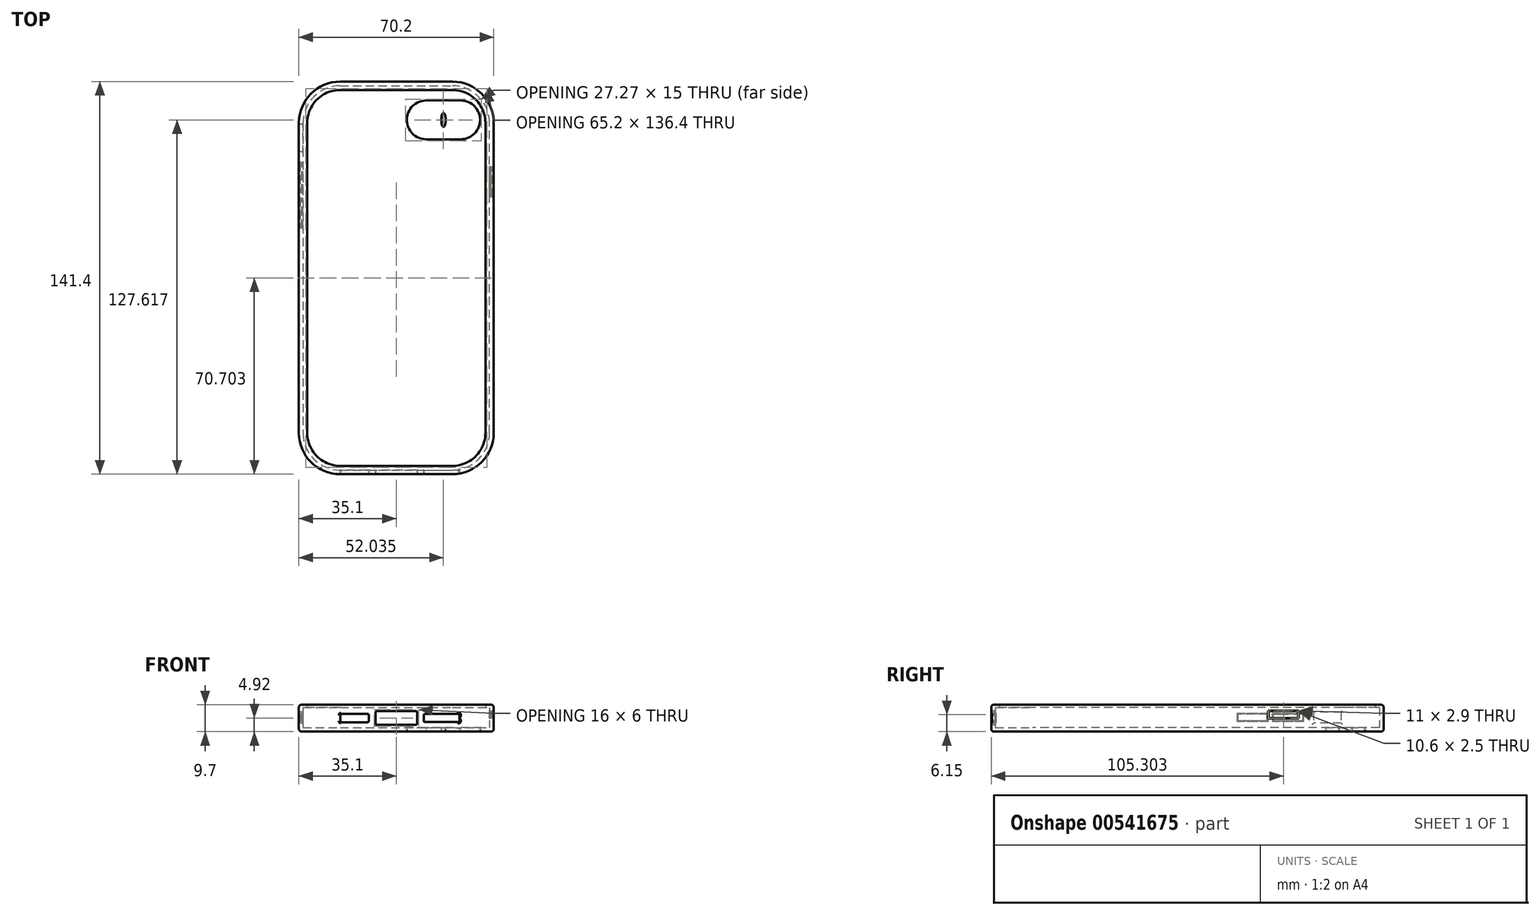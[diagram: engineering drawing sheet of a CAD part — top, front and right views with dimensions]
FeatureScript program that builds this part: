
annotation { "Feature Type Name" : "Feature", "Feature Type Description" : "" }
export const myFeature = defineFeature(function(context is Context, id is Id, definition is map)
    precondition{}
    {
        {
            var Q0;
            Q0=qCreatedBy(makeId("Top.planeOp"),FACE);
            var sketch = newSketch(context, id + "F0", { "sketchPlane" : qUnion([Q0])});
            skArc(sketch, "E0", {"start": v(-23.7, 70.7) * mm, "mid": v(-33.18, 66.77) * mm, "end": v(-37.1, 57.3) * mm});
            skArc(sketch, "E1", {"start": v(-37.1, -54.3) * mm, "mid": v(-33.18, -63.78) * mm, "end": v(-23.7, -67.7) * mm});
            skArc(sketch, "E2", {"start": v(16.7, -67.7) * mm, "mid": v(26.18, -63.78) * mm, "end": v(30.1, -54.3) * mm});
            skArc(sketch, "E3", {"start": v(30.1, 57.3) * mm, "mid": v(26.18, 66.77) * mm, "end": v(16.7, 70.7) * mm});
            skLineSegment(sketch, "E4", {"start": v(-23.7, -67.7) * mm, "end": v(16.7, -67.7) * mm});
            skLineSegment(sketch, "E5", {"start": v(30.1, -54.3) * mm, "end": v(30.1, 57.3) * mm});
            skLineSegment(sketch, "E6", {"start": v(-37.1, 57.3) * mm, "end": v(-37.1, -54.3) * mm});
            skLineSegment(sketch, "E7", {"start": v(-23.7, 70.7) * mm, "end": v(16.7, 70.7) * mm});
            skLineSegment(sketch, "E8.0", {"start": v(-23.7, 72.2) * mm, "end": v(16.7, 72.2) * mm});
            skArc(sketch, "E8.1", {"start": v(31.6, 57.3) * mm, "mid": v(27.24, 67.83) * mm, "end": v(16.7, 72.2) * mm});
            skArc(sketch, "E8.2", {"start": v(-23.7, 72.2) * mm, "mid": v(-34.24, 67.83) * mm, "end": v(-38.6, 57.3) * mm});
            skLineSegment(sketch, "E8.3", {"start": v(31.6, -54.3) * mm, "end": v(31.6, 57.3) * mm});
            skLineSegment(sketch, "E8.4", {"start": v(-38.6, 57.3) * mm, "end": v(-38.6, -54.3) * mm});
            skArc(sketch, "E8.5", {"start": v(-38.6, -54.3) * mm, "mid": v(-34.24, -64.84) * mm, "end": v(-23.7, -69.2) * mm});
            skLineSegment(sketch, "E8.6", {"start": v(-23.7, -69.2) * mm, "end": v(16.7, -69.2) * mm});
            skArc(sketch, "E8.7", {"start": v(16.7, -69.2) * mm, "mid": v(27.24, -64.84) * mm, "end": v(31.6, -54.3) * mm});
            skLineSegment(sketch, "E9", {"start": v(-37.1, -54.3) * mm, "end": v(-3.5, -54.3) * mm, "construction": true});
            skLineSegment(sketch, "E10", {"start": v(-3.5, -54.3) * mm, "end": v(-3.5, -67.7) * mm, "construction": true});
            skSolve(sketch);
        }
        {
            var Q0;
            Q0=makeQuery(id+"F0.imprint","IMPRINT",FACE,{"disambiguationData":[TD([[makeQuery(id+"F0.imprint","IMPRINT",EDGE,{"derivedFrom":sQuery(id+"F0.wireOp",EDGE,"E0")}),-1.0]])]});
            extrude(context, id + "F1", {"entities" : qUnion([Q0]), "depth" : 8.2 * mm, "offsetDistance" : 25 * mm});
        }
        {
            var Q0;
            Q0=makeQuery(id+"F0.imprint","IMPRINT",FACE,{"disambiguationData":[TD([[makeQuery(id+"F0.imprint","IMPRINT",EDGE,{"derivedFrom":sQuery(id+"F0.wireOp",EDGE,"E0")}),1.0]])]});
            var Q1;
            Q1=makeQuery(id+"F0.imprint","IMPRINT",FACE,{"disambiguationData":[TD([[makeQuery(id+"F0.imprint","IMPRINT",EDGE,{"derivedFrom":sQuery(id+"F0.wireOp",EDGE,"E0")}),-1.0]])]});
            extrude(context, id + "F2", {"entities" : qUnion([Q0, Q1]), "operationType" : NewBodyOperationType.ADD, "oppositeDirection" : true, "depth" : 1.5 * mm, "offsetDistance" : 25 * mm});
        }
        {
            var Q0;
            {var subQ0=sQuery(id+"F0.wireOp",EDGE,"E8.6");Q0=makeQuery(id+"F2.boolean.opBoolean","MERGE",FACE,{"derivedFrom":[makeQuery(id+"F1.opExtrude","SWEPT_FACE",FACE,{"disambiguationData":[OSD([subQ0])]}),makeQuery(id+"F2.opExtrude","SWEPT_FACE",FACE,{"disambiguationData":[OSD([subQ0])]})]});}
            var sketch = newSketch(context, id + "F3", { "sketchPlane" : qUnion([Q0])});
            skLineSegment(sketch, "E11", {"start": v(-23.7, 3.42) * mm, "end": v(16.7, 3.42) * mm, "construction": true});
            skLineSegment(sketch, "E12", {"start": v(-3.5, -1.5) * mm, "end": v(-3.5, 8.2) * mm, "construction": true});
            skLineSegment(sketch, "E13.bottom", {"start": v(-11, 5.92) * mm, "end": v(4, 5.92) * mm});
            skLineSegment(sketch, "E13.top", {"start": v(-11, 0.92) * mm, "end": v(4, 0.92) * mm});
            skLineSegment(sketch, "E13.left", {"start": v(-11, 5.92) * mm, "end": v(-11, 0.92) * mm});
            skLineSegment(sketch, "E13.right", {"start": v(4, 5.92) * mm, "end": v(4, 0.92) * mm});
            skPoint(sketch, "E13.middle", {"position": v(-3.5, 3.42) * mm});
            skLineSegment(sketch, "E14.bottom", {"start": v(-23.7, 3.42) * mm, "end": v(-10.9, 3.42) * mm});
            skLineSegment(sketch, "E14.top", {"start": v(-26.2, 4.92) * mm, "end": v(-13.4, 4.92) * mm});
            skLineSegment(sketch, "E14.left", {"start": v(-26.2, 3.42) * mm, "end": v(-26.2, 4.92) * mm});
            skLineSegment(sketch, "E14.right", {"start": v(-13.4, 3.42) * mm, "end": v(-13.4, 4.92) * mm});
            skLineSegment(sketch, "E15.top", {"start": v(-26.2, 1.87) * mm, "end": v(-13.4, 1.87) * mm});
            skLineSegment(sketch, "E15.left", {"start": v(-26.2, 3.42) * mm, "end": v(-26.2, 1.87) * mm});
            skLineSegment(sketch, "E15.right", {"start": v(-13.4, 3.42) * mm, "end": v(-13.4, 1.87) * mm});
            skLineSegment(sketch, "E16.bottom", {"start": v(19.2, 3.42) * mm, "end": v(6.4, 3.42) * mm});
            skLineSegment(sketch, "E16.top", {"start": v(19.2, 4.92) * mm, "end": v(6.4, 4.92) * mm});
            skLineSegment(sketch, "E16.left", {"start": v(19.2, 3.42) * mm, "end": v(19.2, 4.92) * mm});
            skLineSegment(sketch, "E16.right", {"start": v(6.4, 3.42) * mm, "end": v(6.4, 4.92) * mm});
            skLineSegment(sketch, "E17.top", {"start": v(19.2, 1.92) * mm, "end": v(6.4, 1.92) * mm});
            skLineSegment(sketch, "E17.left", {"start": v(19.2, 3.42) * mm, "end": v(19.2, 1.92) * mm});
            skLineSegment(sketch, "E17.right", {"start": v(6.4, 3.42) * mm, "end": v(6.4, 1.92) * mm});
            skSolve(sketch);
        }
        {
            var Q0;
            Q0=makeQuery(id+"F3.imprint","IMPRINT",FACE,{"disambiguationData":[TD([[makeQuery(id+"F3.imprint","IMPRINT",EDGE,{"derivedFrom":sQuery(id+"F3.wireOp",EDGE,"E14.bottom")}),-1.0]])]});
            var Q1;
            Q1=makeQuery(id+"F3.imprint","IMPRINT",FACE,{"disambiguationData":[TD([[makeQuery(id+"F3.imprint","IMPRINT",EDGE,{"derivedFrom":sQuery(id+"F3.wireOp",EDGE,"E14.top")}),-1.0]])]});
            var Q2;
            Q2=makeQuery(id+"F3.imprint","IMPRINT",FACE,{"disambiguationData":[TD([[makeQuery(id+"F3.imprint","IMPRINT",EDGE,{"derivedFrom":sQuery(id+"F3.wireOp",EDGE,"E13.bottom")}),-1.0]])]});
            var Q3;
            Q3=makeQuery(id+"F3.imprint","IMPRINT",FACE,{"disambiguationData":[TD([[makeQuery(id+"F3.imprint","IMPRINT",EDGE,{"derivedFrom":sQuery(id+"F3.wireOp",EDGE,"E16.top")}),1.0]])]});
            var Q4;
            Q4=makeQuery(id+"F3.imprint","IMPRINT",FACE,{"disambiguationData":[TD([[makeQuery(id+"F3.imprint","IMPRINT",EDGE,{"derivedFrom":sQuery(id+"F3.wireOp",EDGE,"E16.bottom")}),1.0]])]});
            extrude(context, id + "F4", {"entities" : qUnion([Q0, Q1, Q2, Q3, Q4]), "operationType" : NewBodyOperationType.REMOVE, "oppositeDirection" : true, "depth" : 3 * mm, "offsetDistance" : 25 * mm});
        }
        {
            var Q0;
            Q0=makeQuery(id+"F2.opExtrude","CAP_FACE",FACE,{"disambiguationData":[OSD([sQuery(id+"F0.wireOp",EDGE,"E8.0"),sQuery(id+"F0.wireOp",EDGE,"E8.1"),sQuery(id+"F0.wireOp",EDGE,"E8.2"),sQuery(id+"F0.wireOp",EDGE,"E8.3"),sQuery(id+"F0.wireOp",EDGE,"E8.4"),sQuery(id+"F0.wireOp",EDGE,"E8.5"),sQuery(id+"F0.wireOp",EDGE,"E8.6"),sQuery(id+"F0.wireOp",EDGE,"E8.7")])],"isStart":false});
            var sketch = newSketch(context, id + "F5", { "sketchPlane" : qUnion([Q0])});
            skCircle(sketch, "E18", {"center": v(19.7, -58.4) * mm, "radius": 7 * mm});
            skCircle(sketch, "E19.1.0.0", {"center": v(7.3, -58.4) * mm, "radius": 7 * mm});
            skLineSegment(sketch, "E19.direction1", {"start": v(19.7, -58.4) * mm, "end": v(7.3, -58.4) * mm, "construction": true});
            skLineSegment(sketch, "E20", {"start": v(19.75, -65.4) * mm, "end": v(7.3, -65.4) * mm});
            skLineSegment(sketch, "E21", {"start": v(7.2, -51.4) * mm, "end": v(19.7, -51.4) * mm});
            skSolve(sketch);
        }
        {
            var Q0;
            {var subQ0=sQuery(id+"F5.wireOp",EDGE,"E18");var subQ3=makeQuery(id+"F5.imprint","IMPRINT",VERTEX,{"derivedFrom":subQ0});Q0=makeQuery(id+"F5.imprint","IMPRINT",FACE,{"disambiguationData":[TD([[makeQuery(id+"F5.imprint","IMPRINT",EDGE,{"disambiguationData":[TD([[subQ3,1.0]])],"derivedFrom":subQ0}),1.0]])]});}
            var Q1;
            {var subQ0=sQuery(id+"F5.wireOp",EDGE,"E19.1.0.0");var subQ1=makeQuery(id+"F5.imprint","INTERSECT",VERTEX,{"derivedFrom":[subQ0,sQuery(id+"F5.wireOp",EDGE,"E20")]});Q1=makeQuery(id+"F5.imprint","IMPRINT",FACE,{"disambiguationData":[TD([[makeQuery(id+"F5.imprint","IMPRINT",EDGE,{"disambiguationData":[TD([[subQ1,1.0]])],"derivedFrom":subQ0}),1.0]])]});}
            var Q2;
            {var subQ0=sQuery(id+"F5.wireOp",EDGE,"E20");Q2=makeQuery(id+"F5.imprint","IMPRINT",FACE,{"disambiguationData":[TD([[makeQuery(id+"F5.imprint","IMPRINT",EDGE,{"derivedFrom":subQ0}),-1.0]])]});}
            var Q3;
            {var subQ0=sQuery(id+"F5.wireOp",EDGE,"E19.1.0.0");var subQ1=sQuery(id+"F5.wireOp",EDGE,"E18");var subQ2=makeQuery(id+"F5.imprint","INTERSECT",VERTEX,{"disambiguationData":[OD(0.0)],"derivedFrom":[subQ1,subQ0]});Q3=makeQuery(id+"F5.imprint","IMPRINT",FACE,{"disambiguationData":[TD([[makeQuery(id+"F5.imprint","IMPRINT",EDGE,{"disambiguationData":[TD([[subQ2,-1.0]])],"derivedFrom":subQ1}),1.0]])]});}
            var Q4;
            {var subQ0=sQuery(id+"F5.wireOp",EDGE,"E21");var subQ1=sQuery(id+"F5.wireOp",EDGE,"E18");var subQ2=makeQuery(id+"F5.imprint","INTERSECT",VERTEX,{"derivedFrom":[subQ1,subQ0]});Q4=makeQuery(id+"F5.imprint","IMPRINT",FACE,{"disambiguationData":[TD([[makeQuery(id+"F5.imprint","IMPRINT",EDGE,{"disambiguationData":[TD([[subQ2,-1.0]])],"derivedFrom":subQ1}),-1.0]])]});}
            extrude(context, id + "F6", {"entities" : qUnion([Q0, Q1, Q2, Q3, Q4]), "operationType" : NewBodyOperationType.REMOVE, "oppositeDirection" : true, "depth" : 5 * mm, "offsetDistance" : 25 * mm});
        }
        {
            var Q0;
            Q0=makeQuery(id+"F1.opExtrude","SWEPT_FACE",FACE,{"disambiguationData":[OSD([sQuery(id+"F0.wireOp",EDGE,"E5")])]});
            var sketch = newSketch(context, id + "F7", { "sketchPlane" : qUnion([Q0])});
            skLineSegment(sketch, "E22", {"start": v(-57.3, 4.65) * mm, "end": v(-33.08, 4.65) * mm, "construction": true});
            skLineSegment(sketch, "E23", {"start": v(-36.1, 8.2) * mm, "end": v(-36.1, 0) * mm, "construction": true});
            skLineSegment(sketch, "E24.bottom", {"start": v(-36.1, 4.65) * mm, "end": v(-41.4, 4.65) * mm});
            skLineSegment(sketch, "E24.top", {"start": v(-36.1, 5.9) * mm, "end": v(-41.4, 5.9) * mm});
            skLineSegment(sketch, "E24.left", {"start": v(-36.1, 4.65) * mm, "end": v(-36.1, 5.9) * mm});
            skLineSegment(sketch, "E24.right", {"start": v(-41.4, 4.65) * mm, "end": v(-41.4, 5.9) * mm});
            skLineSegment(sketch, "E25.top", {"start": v(-36.1, 3.4) * mm, "end": v(-41.4, 3.4) * mm});
            skLineSegment(sketch, "E25.left", {"start": v(-36.1, 4.65) * mm, "end": v(-36.1, 3.4) * mm});
            skLineSegment(sketch, "E25.right", {"start": v(-41.4, 4.65) * mm, "end": v(-41.4, 3.4) * mm});
            skLineSegment(sketch, "E26.bottom", {"start": v(-41.4, 5.9) * mm, "end": v(-30.8, 5.9) * mm});
            skLineSegment(sketch, "E26.top", {"start": v(-41.4, 3.4) * mm, "end": v(-30.8, 3.4) * mm});
            skLineSegment(sketch, "E26.right", {"start": v(-30.8, 5.9) * mm, "end": v(-30.8, 3.4) * mm});
            skPoint(sketch, "E26.middle", {"position": v(-36.1, 4.65) * mm});
            skLineSegment(sketch, "E27.0", {"start": v(-41.6, 6.1) * mm, "end": v(-30.6, 6.1) * mm});
            skLineSegment(sketch, "E27.1", {"start": v(-41.6, 4.65) * mm, "end": v(-41.6, 6.1) * mm});
            skLineSegment(sketch, "E27.2", {"start": v(-30.6, 6.1) * mm, "end": v(-30.6, 3.2) * mm});
            skLineSegment(sketch, "E27.3", {"start": v(-41.6, 3.2) * mm, "end": v(-30.6, 3.2) * mm});
            skLineSegment(sketch, "E27.4", {"start": v(-41.6, 4.65) * mm, "end": v(-41.6, 3.2) * mm});
            skSolve(sketch);
        }
        {
            var Q0;
            {var subQ4=sQuery(id+"F7.wireOp",EDGE,"E24.right");Q0=makeQuery(id+"F7.imprint","IMPRINT",FACE,{"disambiguationData":[TD([[makeQuery(id+"F7.imprint","IMPRINT",EDGE,{"derivedFrom":subQ4}),1.0]])]});}
            extrude(context, id + "F8", {"entities" : qUnion([Q0]), "operationType" : NewBodyOperationType.REMOVE, "oppositeDirection" : true, "depth" : .5 * mm, "offsetDistance" : 25 * mm});
        }
        {
            var Q0;
            {var subQ0=sQuery(id+"F0.wireOp",EDGE,"E8.3");Q0=makeQuery(id+"F2.boolean.opBoolean","MERGE",FACE,{"derivedFrom":[makeQuery(id+"F1.opExtrude","SWEPT_FACE",FACE,{"disambiguationData":[OSD([subQ0])]}),makeQuery(id+"F2.opExtrude","SWEPT_FACE",FACE,{"disambiguationData":[OSD([subQ0])]})]});}
            var sketch = newSketch(context, id + "F9", { "sketchPlane" : qUnion([Q0])});
            skLineSegment(sketch, "E28.bottom", {"start": v(30.8, 5.9) * mm, "end": v(41.4, 5.9) * mm});
            skLineSegment(sketch, "E28.top", {"start": v(30.8, 3.4) * mm, "end": v(41.4, 3.4) * mm});
            skLineSegment(sketch, "E28.right", {"start": v(41.4, 5.9) * mm, "end": v(41.4, 3.4) * mm});
            skLineSegment(sketch, "E29", {"start": v(30.8, 5.9) * mm, "end": v(30.8, 3.4) * mm});
            skLineSegment(sketch, "E30.0", {"start": v(41.6, 6.1) * mm, "end": v(41.6, 3.2) * mm});
            skLineSegment(sketch, "E30.1", {"start": v(30.6, 6.1) * mm, "end": v(41.6, 6.1) * mm});
            skLineSegment(sketch, "E30.2", {"start": v(30.6, 6.1) * mm, "end": v(30.6, 3.2) * mm});
            skLineSegment(sketch, "E30.3", {"start": v(30.6, 3.2) * mm, "end": v(41.6, 3.2) * mm});
            skLineSegment(sketch, "E31.0", {"start": v(-59.3, 13.2) * mm, "end": v(-59.3, -6.5) * mm});
            skLineSegment(sketch, "E31.1", {"start": v(62.3, 13.2) * mm, "end": v(-59.3, 13.2) * mm});
            skLineSegment(sketch, "E31.2", {"start": v(62.3, -6.5) * mm, "end": v(62.3, 13.2) * mm});
            skLineSegment(sketch, "E31.3", {"start": v(-59.3, -6.5) * mm, "end": v(62.3, -6.5) * mm});
            skSolve(sketch);
        }
        {
            var Q0;
            Q0=makeQuery(id+"F9.imprint","IMPRINT",FACE,{"disambiguationData":[TD([[makeQuery(id+"F9.imprint","IMPRINT",EDGE,{"derivedFrom":sQuery(id+"F9.wireOp",EDGE,"E28.bottom")}),1.0]])]});
            extrude(context, id + "F10", {"entities" : qUnion([Q0]), "operationType" : NewBodyOperationType.REMOVE, "oppositeDirection" : true, "depth" : .5 * mm, "offsetDistance" : 25 * mm});
        }
        {
            var Q0;
            {var subQ0=sQuery(id+"F0.wireOp",EDGE,"E8.4");Q0=makeQuery(id+"F2.boolean.opBoolean","MERGE",FACE,{"derivedFrom":[makeQuery(id+"F1.opExtrude","SWEPT_FACE",FACE,{"disambiguationData":[OSD([subQ0])]}),makeQuery(id+"F2.opExtrude","SWEPT_FACE",FACE,{"disambiguationData":[OSD([subQ0])]})]});}
            var sketch = newSketch(context, id + "F11", { "sketchPlane" : qUnion([Q0])});
            skLineSegment(sketch, "E32", {"start": v(-66.46, 3.55) * mm, "end": v(7.63, 3.55) * mm, "construction": true});
            skLineSegment(sketch, "E33", {"start": v(-56.9, 8.2) * mm, "end": v(-56.9, 0) * mm, "construction": true});
            skLineSegment(sketch, "E34.bottom", {"start": v(-56.9, 3.55) * mm, "end": v(-46.9, 3.55) * mm});
            skLineSegment(sketch, "E34.top", {"start": v(-56.9, 5.55) * mm, "end": v(-46.9, 5.55) * mm});
            skLineSegment(sketch, "E34.left", {"start": v(-56.9, 3.55) * mm, "end": v(-56.9, 5.55) * mm});
            skLineSegment(sketch, "E34.right", {"start": v(-46.9, 3.55) * mm, "end": v(-46.9, 5.55) * mm});
            skLineSegment(sketch, "E35.top", {"start": v(-56.9, 1.55) * mm, "end": v(-46.9, 1.55) * mm});
            skLineSegment(sketch, "E35.left", {"start": v(-56.9, 5.55) * mm, "end": v(-56.9, 1.55) * mm});
            skLineSegment(sketch, "E35.right", {"start": v(-46.9, 5.55) * mm, "end": v(-46.9, 1.55) * mm});
            skLineSegment(sketch, "E36", {"start": v(-37.63, 8.2) * mm, "end": v(-37.63, 0) * mm, "construction": true});
            skLineSegment(sketch, "E37.bottom", {"start": v(-42.98, 4.8) * mm, "end": v(-32.28, 4.8) * mm});
            skLineSegment(sketch, "E37.top", {"start": v(-42.98, 2.3) * mm, "end": v(-32.28, 2.3) * mm});
            skLineSegment(sketch, "E37.left", {"start": v(-42.98, 4.8) * mm, "end": v(-42.98, 2.3) * mm});
            skPoint(sketch, "E37.middle", {"position": v(-37.63, 3.55) * mm});
            skLineSegment(sketch, "E38.bottom", {"start": v(-30.28, 4.8) * mm, "end": v(-19.58, 4.8) * mm});
            skLineSegment(sketch, "E38.top", {"start": v(-30.28, 2.3) * mm, "end": v(-19.58, 2.3) * mm});
            skLineSegment(sketch, "E38.left", {"start": v(-30.28, 4.8) * mm, "end": v(-30.28, 2.3) * mm});
            skLineSegment(sketch, "E38.right", {"start": v(-19.58, 4.8) * mm, "end": v(-19.58, 2.3) * mm});
            skPoint(sketch, "E38.middle", {"position": v(-24.93, 3.55) * mm});
            skLineSegment(sketch, "E39", {"start": v(-32.28, 4.8) * mm, "end": v(-32.28, 2.3) * mm});
            skLineSegment(sketch, "E40.0", {"start": v(-43.18, 5) * mm, "end": v(-32.08, 5) * mm});
            skLineSegment(sketch, "E40.1", {"start": v(-43.18, 5) * mm, "end": v(-43.18, 2.1) * mm});
            skLineSegment(sketch, "E40.2", {"start": v(-43.18, 2.1) * mm, "end": v(-32.08, 2.1) * mm});
            skLineSegment(sketch, "E40.3", {"start": v(-32.08, 5) * mm, "end": v(-32.08, 2.1) * mm});
            skLineSegment(sketch, "E41.0", {"start": v(-30.48, 2.1) * mm, "end": v(-19.38, 2.1) * mm});
            skLineSegment(sketch, "E41.1", {"start": v(-30.48, 5) * mm, "end": v(-30.48, 2.1) * mm});
            skLineSegment(sketch, "E41.2", {"start": v(-30.48, 5) * mm, "end": v(-19.38, 5) * mm});
            skLineSegment(sketch, "E41.3", {"start": v(-19.38, 5) * mm, "end": v(-19.38, 2.1) * mm});
            skSolve(sketch);
        }
        {
            var Q0;
            {var subQ0=sQuery(id+"F11.wireOp",EDGE,"E34.bottom");Q0=makeQuery(id+"F11.imprint","IMPRINT",FACE,{"disambiguationData":[TD([[makeQuery(id+"F11.imprint","IMPRINT",EDGE,{"derivedFrom":subQ0}),-1.0]])]});}
            var Q1;
            {var subQ0=sQuery(id+"F11.wireOp",EDGE,"E34.bottom");Q1=makeQuery(id+"F11.imprint","IMPRINT",FACE,{"disambiguationData":[TD([[makeQuery(id+"F11.imprint","IMPRINT",EDGE,{"derivedFrom":subQ0}),1.0]])]});}
            extrude(context, id + "F12", {"entities" : qUnion([Q0, Q1]), "operationType" : NewBodyOperationType.REMOVE, "oppositeDirection" : true, "depth" : 5 * mm, "offsetDistance" : 25 * mm});
        }
        {
            var Q0;
            Q0=makeQuery(id+"F11.imprint","IMPRINT",FACE,{"disambiguationData":[TD([[makeQuery(id+"F11.imprint","IMPRINT",EDGE,{"derivedFrom":sQuery(id+"F11.wireOp",EDGE,"E37.bottom")}),1.0]])]});
            var Q1;
            Q1=makeQuery(id+"F11.imprint","IMPRINT",FACE,{"disambiguationData":[TD([[makeQuery(id+"F11.imprint","IMPRINT",EDGE,{"derivedFrom":sQuery(id+"F11.wireOp",EDGE,"E38.bottom")}),1.0]])]});
            extrude(context, id + "F13", {"entities" : qUnion([Q0, Q1]), "operationType" : NewBodyOperationType.REMOVE, "oppositeDirection" : true, "depth" : .5 * mm, "offsetDistance" : 25 * mm});
        }
        {
            var Q0;
            Q0=makeQuery(id+"F1.opExtrude","SWEPT_FACE",FACE,{"disambiguationData":[OSD([sQuery(id+"F0.wireOp",EDGE,"E6")])]});
            var sketch = newSketch(context, id + "F14", { "sketchPlane" : qUnion([Q0])});
            skLineSegment(sketch, "E42.bottom", {"start": v(19.58, 4.99) * mm, "end": v(30.07, 4.99) * mm});
            skLineSegment(sketch, "E42.top", {"start": v(19.58, 2.49) * mm, "end": v(30.07, 2.49) * mm});
            skLineSegment(sketch, "E42.left", {"start": v(19.58, 4.99) * mm, "end": v(19.58, 2.49) * mm});
            skPoint(sketch, "E42.middle", {"position": v(24.83, 3.74) * mm});
            skLineSegment(sketch, "E43.bottom", {"start": v(32.28, 4.99) * mm, "end": v(42.98, 4.99) * mm});
            skLineSegment(sketch, "E43.top", {"start": v(32.28, 2.49) * mm, "end": v(42.98, 2.49) * mm});
            skLineSegment(sketch, "E43.left", {"start": v(32.28, 4.99) * mm, "end": v(32.28, 2.49) * mm});
            skLineSegment(sketch, "E43.right", {"start": v(42.98, 4.99) * mm, "end": v(42.98, 2.49) * mm});
            skPoint(sketch, "E43.middle", {"position": v(37.63, 3.74) * mm});
            skLineSegment(sketch, "E44", {"start": v(30.07, 4.99) * mm, "end": v(30.07, 2.49) * mm});
            skLineSegment(sketch, "E45.0", {"start": v(19.38, 5.19) * mm, "end": v(30.27, 5.19) * mm});
            skLineSegment(sketch, "E45.1", {"start": v(19.38, 5.19) * mm, "end": v(19.38, 2.29) * mm});
            skLineSegment(sketch, "E45.2", {"start": v(19.38, 2.29) * mm, "end": v(30.27, 2.29) * mm});
            skLineSegment(sketch, "E45.3", {"start": v(30.27, 5.19) * mm, "end": v(30.27, 2.29) * mm});
            skLineSegment(sketch, "E46.0", {"start": v(32.08, 2.29) * mm, "end": v(43.18, 2.29) * mm});
            skLineSegment(sketch, "E46.1", {"start": v(32.08, 5.19) * mm, "end": v(32.08, 2.29) * mm});
            skLineSegment(sketch, "E46.2", {"start": v(32.08, 5.19) * mm, "end": v(43.18, 5.19) * mm});
            skLineSegment(sketch, "E46.3", {"start": v(43.18, 5.19) * mm, "end": v(43.18, 2.29) * mm});
            skSolve(sketch);
        }
        {
            var Q0;
            Q0=makeQuery(id+"F14.imprint","IMPRINT",FACE,{"disambiguationData":[TD([[makeQuery(id+"F14.imprint","IMPRINT",EDGE,{"derivedFrom":sQuery(id+"F14.wireOp",EDGE,"E42.bottom")}),1.0]])]});
            var Q1;
            Q1=makeQuery(id+"F14.imprint","IMPRINT",FACE,{"disambiguationData":[TD([[makeQuery(id+"F14.imprint","IMPRINT",EDGE,{"derivedFrom":sQuery(id+"F14.wireOp",EDGE,"E43.bottom")}),1.0]])]});
            extrude(context, id + "F15", {"entities" : qUnion([Q0, Q1]), "operationType" : NewBodyOperationType.REMOVE, "oppositeDirection" : true, "depth" : .5 * mm, "offsetDistance" : 25 * mm});
        }
        {
            var Q0;
            Q0=makeQuery(id+"F1.opExtrude","CAP_FACE",FACE,{"disambiguationData":[OSD([sQuery(id+"F0.wireOp",EDGE,"E0"),sQuery(id+"F0.wireOp",EDGE,"E1"),sQuery(id+"F0.wireOp",EDGE,"E2"),sQuery(id+"F0.wireOp",EDGE,"E3"),sQuery(id+"F0.wireOp",EDGE,"E4"),sQuery(id+"F0.wireOp",EDGE,"E5"),sQuery(id+"F0.wireOp",EDGE,"E6"),sQuery(id+"F0.wireOp",EDGE,"E7"),sQuery(id+"F0.wireOp",EDGE,"E8.0"),sQuery(id+"F0.wireOp",EDGE,"E8.1"),sQuery(id+"F0.wireOp",EDGE,"E8.2"),sQuery(id+"F0.wireOp",EDGE,"E8.3"),sQuery(id+"F0.wireOp",EDGE,"E8.4"),sQuery(id+"F0.wireOp",EDGE,"E8.5"),sQuery(id+"F0.wireOp",EDGE,"E8.6"),sQuery(id+"F0.wireOp",EDGE,"E8.7")])],"isStart":false});
            var sketch = newSketch(context, id + "F16", { "sketchPlane" : qUnion([Q0])});
            skArc(sketch, "E47", {"start": v(-23.7, 70.7) * mm, "mid": v(-33.18, 66.77) * mm, "end": v(-37.1, 57.3) * mm});
            skArc(sketch, "E48", {"start": v(16.7, -67.7) * mm, "mid": v(26.18, -63.78) * mm, "end": v(30.1, -54.3) * mm});
            skArc(sketch, "E49", {"start": v(30.1, 57.3) * mm, "mid": v(26.18, 66.77) * mm, "end": v(16.7, 70.7) * mm});
            skLineSegment(sketch, "E50", {"start": v(-23.7, -67.7) * mm, "end": v(16.7, -67.7) * mm});
            skLineSegment(sketch, "E51", {"start": v(30.1, -54.3) * mm, "end": v(30.1, 57.3) * mm});
            skLineSegment(sketch, "E52", {"start": v(-37.1, 57.3) * mm, "end": v(-37.1, -54.3) * mm});
            skLineSegment(sketch, "E53", {"start": v(-23.7, 70.7) * mm, "end": v(16.7, 70.7) * mm});
            skLineSegment(sketch, "E54", {"start": v(-37.1, -54.3) * mm, "end": v(-3.5, -54.3) * mm, "construction": true});
            skLineSegment(sketch, "E55", {"start": v(-3.5, -54.3) * mm, "end": v(-3.5, -67.7) * mm, "construction": true});
            skArc(sketch, "E56.0", {"start": v(16.7, -66.2) * mm, "mid": v(25.11, -62.72) * mm, "end": v(28.6, -54.3) * mm});
            skLineSegment(sketch, "E56.1", {"start": v(-23.81, -66.2) * mm, "end": v(16.7, -66.2) * mm});
            skLineSegment(sketch, "E56.2", {"start": v(28.6, -54.3) * mm, "end": v(28.6, 57.3) * mm});
            skArc(sketch, "E56.4", {"start": v(28.6, 57.3) * mm, "mid": v(25.11, 65.7) * mm, "end": v(16.7, 69.2) * mm});
            skLineSegment(sketch, "E56.5", {"start": v(-23.7, 69.2) * mm, "end": v(16.7, 69.2) * mm});
            skArc(sketch, "E56.6", {"start": v(-23.7, 69.2) * mm, "mid": v(-32.11, 65.7) * mm, "end": v(-35.6, 57.3) * mm});
            skLineSegment(sketch, "E56.7", {"start": v(-35.6, 57.3) * mm, "end": v(-35.6, -54.42) * mm});
            skArc(sketch, "E57", {"start": v(-37.1, -54.3) * mm, "mid": v(-33.18, -63.78) * mm, "end": v(-23.7, -67.7) * mm});
            skArc(sketch, "E58.0", {"start": v(-35.6, -54.3) * mm, "mid": v(-32.11, -62.72) * mm, "end": v(-23.7, -66.2) * mm});
            skSolve(sketch);
        }
        {
            var Q0;
            Q0=makeQuery(id+"F16.imprint","IMPRINT",FACE,{"disambiguationData":[TD([[makeQuery(id+"F16.imprint","IMPRINT",EDGE,{"derivedFrom":sQuery(id+"F16.wireOp",EDGE,"E47")}),1.0]])]});
            extrude(context, id + "F17", {"entities" : qUnion([Q0]), "operationType" : NewBodyOperationType.ADD, "oppositeDirection" : true, "depth" : 1 * mm, "offsetDistance" : 25 * mm});
        }
        {
            var Q0;
            Q0=makeQuery(id+"F17.opExtrude","CAP_EDGE",EDGE,{"disambiguationData":[OSD([sQuery(id+"F16.wireOp",EDGE,"E56.7")])],"isStart":true});
            var Q1;
            Q1=makeQuery(id+"F17.opExtrude","CAP_EDGE",EDGE,{"disambiguationData":[OSD([sQuery(id+"F16.wireOp",EDGE,"E56.7")])],"isStart":false});
            var Q2;
            Q2=makeQuery(id+"F17.opExtrude","CAP_EDGE",EDGE,{"disambiguationData":[OSD([sQuery(id+"F16.wireOp",EDGE,"E56.3")])],"isStart":true});
            var Q3;
            Q3=makeQuery(id+"F17.opExtrude","CAP_EDGE",EDGE,{"disambiguationData":[OSD([sQuery(id+"F16.wireOp",EDGE,"E56.3")])],"isStart":false});
            var Q4;
            Q4=makeQuery(id+"F6.boolean.opBoolean","COPY",FACE,{"derivedFrom":makeQuery(id+"F6.opExtrude","SWEPT_FACE",FACE,{"disambiguationData":[OSD([sQuery(id+"F5.wireOp",EDGE,"E19.1.0.0")])]})});
            var Q5;
            Q5=makeQuery(id+"F12.boolean.opBoolean","COPY",EDGE,{"derivedFrom":makeQuery(id+"F12.opExtrude","CAP_EDGE",EDGE,{"disambiguationData":[OSD([sQuery(id+"F11.wireOp",EDGE,"E35.top")])],"isStart":true})});
            var Q6;
            Q6=makeQuery(id+"F12.boolean.opBoolean","INTERSECT",EDGE,{"derivedFrom":[makeQuery(id+"F1.opExtrude","SWEPT_FACE",FACE,{"disambiguationData":[OSD([sQuery(id+"F0.wireOp",EDGE,"E6")])]}),makeQuery(id+"F12.opExtrude","SWEPT_FACE",FACE,{"disambiguationData":[OSD([sQuery(id+"F11.wireOp",EDGE,"E35.top")])]})]});
            var Q7;
            Q7=makeQuery(id+"F12.boolean.opBoolean","COPY",EDGE,{"derivedFrom":makeQuery(id+"F12.opExtrude","CAP_EDGE",EDGE,{"disambiguationData":[OSD([sQuery(id+"F11.wireOp",EDGE,"E35.right")])],"isStart":true})});
            var Q8;
            Q8=makeQuery(id+"F12.boolean.opBoolean","INTERSECT",EDGE,{"derivedFrom":[makeQuery(id+"F1.opExtrude","SWEPT_FACE",FACE,{"disambiguationData":[OSD([sQuery(id+"F0.wireOp",EDGE,"E6")])]}),makeQuery(id+"F12.opExtrude","SWEPT_FACE",FACE,{"disambiguationData":[OSD([sQuery(id+"F11.wireOp",EDGE,"E35.right")])]})]});
            var Q9;
            Q9=makeQuery(id+"F12.boolean.opBoolean","INTERSECT",EDGE,{"derivedFrom":[makeQuery(id+"F1.opExtrude","SWEPT_FACE",FACE,{"disambiguationData":[OSD([sQuery(id+"F0.wireOp",EDGE,"E6")])]}),makeQuery(id+"F12.opExtrude","SWEPT_FACE",FACE,{"disambiguationData":[OSD([sQuery(id+"F11.wireOp",EDGE,"E35.left")])]})]});
            var Q10;
            Q10=makeQuery(id+"F12.boolean.opBoolean","COPY",EDGE,{"derivedFrom":makeQuery(id+"F12.opExtrude","CAP_EDGE",EDGE,{"disambiguationData":[OSD([sQuery(id+"F11.wireOp",EDGE,"E35.left")])],"isStart":true})});
            var Q11;
            Q11=makeQuery(id+"F12.boolean.opBoolean","INTERSECT",EDGE,{"derivedFrom":[makeQuery(id+"F1.opExtrude","SWEPT_FACE",FACE,{"disambiguationData":[OSD([sQuery(id+"F0.wireOp",EDGE,"E6")])]}),makeQuery(id+"F12.opExtrude","SWEPT_FACE",FACE,{"disambiguationData":[OSD([sQuery(id+"F11.wireOp",EDGE,"E34.top")])]})]});
            var Q12;
            Q12=makeQuery(id+"F12.boolean.opBoolean","COPY",EDGE,{"derivedFrom":makeQuery(id+"F12.opExtrude","CAP_EDGE",EDGE,{"disambiguationData":[OSD([sQuery(id+"F11.wireOp",EDGE,"E34.top")])],"isStart":true})});
            var Q13;
            Q13=makeQuery(id+"F4.boolean.opBoolean","COPY",FACE,{"derivedFrom":makeQuery(id+"F4.opExtrude","SWEPT_FACE",FACE,{"disambiguationData":[OSD([sQuery(id+"F3.wireOp",EDGE,"E13.top")])]})});
            var Q14;
            Q14=makeQuery(id+"F4.boolean.opBoolean","COPY",FACE,{"derivedFrom":makeQuery(id+"F4.opExtrude","SWEPT_FACE",FACE,{"disambiguationData":[OSD([sQuery(id+"F3.wireOp",EDGE,"E13.bottom")])]})});
            var Q15;
            Q15=makeQuery(id+"F4.boolean.opBoolean","COPY",FACE,{"derivedFrom":makeQuery(id+"F4.opExtrude","SWEPT_FACE",FACE,{"disambiguationData":[OSD([sQuery(id+"F0.wireOp",EDGE,"E8.5"),sQuery(id+"F0.wireOp",EDGE,"E8.6")])]})});
            var Q16;
            Q16=makeQuery(id+"F4.boolean.opBoolean","COPY",FACE,{"derivedFrom":makeQuery(id+"F4.opExtrude","SWEPT_FACE",FACE,{"disambiguationData":[OSD([sQuery(id+"F3.wireOp",EDGE,"E14.top")])]})});
            var Q17;
            Q17=makeQuery(id+"F4.boolean.opBoolean","COPY",FACE,{"derivedFrom":makeQuery(id+"F4.opExtrude","SWEPT_FACE",FACE,{"disambiguationData":[OSD([sQuery(id+"F3.wireOp",EDGE,"E14.right"),sQuery(id+"F3.wireOp",EDGE,"E15.right")])]})});
            var Q18;
            Q18=makeQuery(id+"F4.boolean.opBoolean","COPY",FACE,{"derivedFrom":makeQuery(id+"F4.opExtrude","SWEPT_FACE",FACE,{"disambiguationData":[OSD([sQuery(id+"F3.wireOp",EDGE,"E15.top")])]})});
            var Q19;
            Q19=makeQuery(id+"F4.boolean.opBoolean","COPY",FACE,{"derivedFrom":makeQuery(id+"F4.opExtrude","SWEPT_FACE",FACE,{"disambiguationData":[OSD([sQuery(id+"F3.wireOp",EDGE,"E17.top")])]})});
            var Q20;
            Q20=makeQuery(id+"F4.boolean.opBoolean","COPY",FACE,{"derivedFrom":makeQuery(id+"F4.opExtrude","SWEPT_FACE",FACE,{"disambiguationData":[OSD([sQuery(id+"F3.wireOp",EDGE,"E16.top")])]})});
            fillet(context, id + "F18", {"entities" : qUnion([Q0, Q1, Q2, Q3, Q4, Q5, Q6, Q7, Q8, Q9, Q10, Q11, Q12, Q13, Q14, Q15, Q16, Q17, Q18, Q19, Q20]), "radius" : .5 * mm, "tangentPropagation" : true, "allowEdgeOverflow" : false});
        }
        {
            var Q0;
            Q0=makeQuery(id+"F2.opExtrude","CAP_EDGE",EDGE,{"disambiguationData":[OSD([sQuery(id+"F0.wireOp",EDGE,"E8.4")])],"isStart":false});
            var Q1;
            Q1=makeQuery(id+"F1.opExtrude","CAP_EDGE",EDGE,{"disambiguationData":[OSD([sQuery(id+"F0.wireOp",EDGE,"E8.3")])],"isStart":false});
            fillet(context, id + "F19", {"entities" : qUnion([Q0, Q1]), "radius" : 1 * mm, "tangentPropagation" : true, "allowEdgeOverflow" : false});
        }
    });
